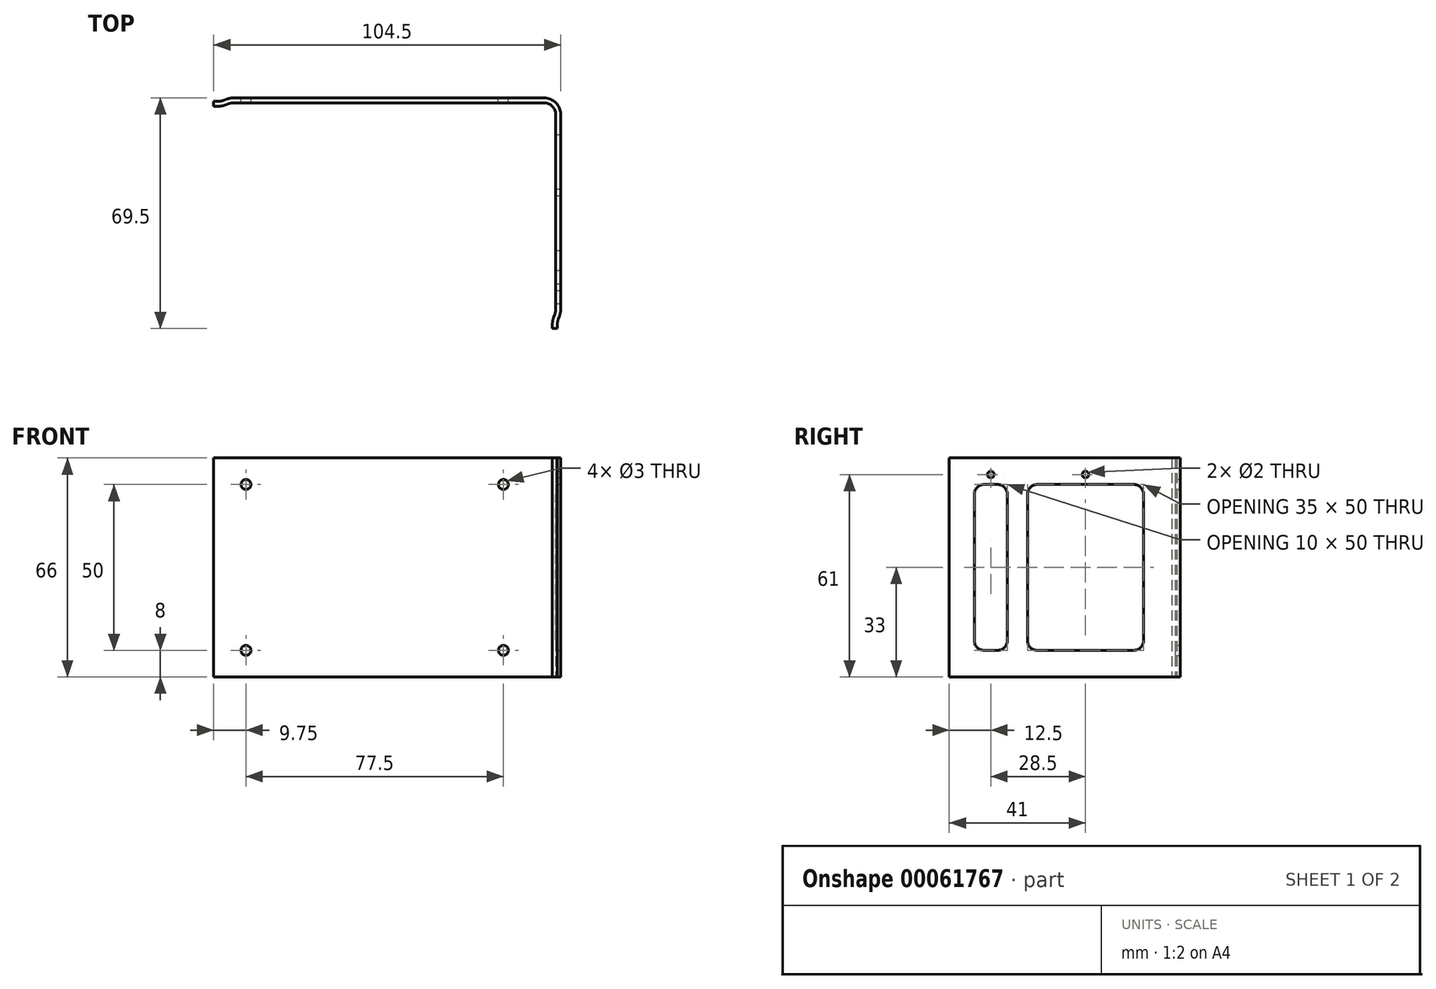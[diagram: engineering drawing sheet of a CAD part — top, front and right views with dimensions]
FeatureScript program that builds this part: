
annotation { "Feature Type Name" : "Feature", "Feature Type Description" : "" }
export const myFeature = defineFeature(function(context is Context, id is Id, definition is map)
    precondition{}
    {
        {
            var Q0;
            Q0=qCreatedBy(makeId("Top.planeOp"),FACE);
            var sketch = newSketch(context, id + "F0", { "sketchPlane" : qUnion([Q0])});
            skLineSegment(sketch, "E0", {"start": v(54.5, -26.49) * mm, "end": v(54.5, 33) * mm});
            skLineSegment(sketch, "E1", {"start": v(-46, 33) * mm, "end": v(-46, 0) * mm});
            skLineSegment(sketch, "E2.0", {"start": v(-47.5, 33) * mm, "end": v(-47.5, 0) * mm});
            skLineSegment(sketch, "E2.3", {"start": v(56, -26.75) * mm, "end": v(56, 33) * mm});
            skLineSegment(sketch, "E2.4", {"start": v(51, 38) * mm, "end": v(-42.5, 38) * mm});
            skLineSegment(sketch, "E3", {"start": v(-46, 0) * mm, "end": v(-47.5, 0) * mm});
            skPoint(sketch, "E4.visualSharp", {"position": v(54.5, 36.5) * mm});
            skArc(sketch, "E4.filletArc", {"start": v(54.5, 33) * mm, "mid": v(53.47, 35.47) * mm, "end": v(51, 36.5) * mm});
            skPoint(sketch, "E5.visualSharp", {"position": v(-46, 36.5) * mm});
            skArc(sketch, "E5.filletArc", {"start": v(-42.5, 36.5) * mm, "mid": v(-44.97, 35.47) * mm, "end": v(-46, 33) * mm});
            skPoint(sketch, "E6.visualSharp", {"position": v(56, 38) * mm});
            skArc(sketch, "E6.filletArc", {"start": v(56, 33) * mm, "mid": v(54.54, 36.54) * mm, "end": v(51, 38) * mm});
            skPoint(sketch, "E7.visualSharp", {"position": v(-47.5, 38) * mm});
            skArc(sketch, "E7.filletArc", {"start": v(-42.5, 38) * mm, "mid": v(-46.04, 36.54) * mm, "end": v(-47.5, 33) * mm});
            skLineSegment(sketch, "E8", {"start": v(54.5, 0) * mm, "end": v(-12.48, 0) * mm, "construction": true});
            skLineSegment(sketch, "E9", {"start": v(0, 36.5) * mm, "end": v(0, -15.2) * mm, "construction": true});
            skLineSegment(sketch, "E10", {"start": v(-42.5, 36.5) * mm, "end": v(51, 36.5) * mm});
            skLineSegment(sketch, "E11", {"start": v(55, -31.5) * mm, "end": v(55, -29.5) * mm});
            skLineSegment(sketch, "E12", {"start": v(55, -29.5) * mm, "end": v(56, -26.75) * mm});
            skLineSegment(sketch, "E13", {"start": v(55, -31.5) * mm, "end": v(53.5, -31.5) * mm});
            skLineSegment(sketch, "E14", {"start": v(53.5, -31.5) * mm, "end": v(53.5, -29.24) * mm});
            skLineSegment(sketch, "E15", {"start": v(53.5, -29.24) * mm, "end": v(54.5, -26.49) * mm});
            skSolve(sketch);
        }
        {
            var Q0;
            Q0=qSketchRegion(id+"F0",true);
            extrude(context, id + "F1", {"entities" : qUnion([Q0]), "depth" : 66 * mm});
        }
        {
            var Q0;
            Q0=makeQuery(id+"F1.opExtrude","SWEPT_FACE",FACE,{"disambiguationData":[OSD([sQuery(id+"F0.wireOp",EDGE,"E2.4")])]});
            var sketch = newSketch(context, id + "F2", { "sketchPlane" : qUnion([Q0])});
            skCircle(sketch, "E16", {"center": v(-38.75, 58) * mm, "radius": 1.5 * mm});
            skLineSegment(sketch, "E17", {"start": v(-38.75, 58) * mm, "end": v(-38.75, 8) * mm, "construction": true});
            skLineSegment(sketch, "E18", {"start": v(-38.75, 8) * mm, "end": v(38.75, 8) * mm, "construction": true});
            skLineSegment(sketch, "E19", {"start": v(38.75, 8) * mm, "end": v(38.75, 58) * mm, "construction": true});
            skLineSegment(sketch, "E20", {"start": v(38.75, 58) * mm, "end": v(-38.75, 58) * mm, "construction": true});
            skCircle(sketch, "E21", {"center": v(-38.75, 8) * mm, "radius": 1.5 * mm});
            skCircle(sketch, "E22", {"center": v(38.75, 8) * mm, "radius": 1.5 * mm});
            skCircle(sketch, "E23", {"center": v(38.75, 58) * mm, "radius": 1.5 * mm});
            skLineSegment(sketch, "E24", {"start": v(0, 0) * mm, "end": v(0, 116) * mm, "construction": true});
            skPoint(sketch, "E24.endSnap0", {"position": v(0, 0) * mm});
            skPoint(sketch, "E25", {"position": v(0, 58) * mm});
            skCircle(sketch, "E26", {"center": v(38.75, 49.63) * mm, "radius": 1.5 * mm});
            skCircle(sketch, "E27", {"center": v(38.75, 16.38) * mm, "radius": 1.5 * mm});
            skLineSegment(sketch, "E28", {"start": v(36, 33) * mm, "end": v(27.19, 33) * mm, "construction": true});
            skSolve(sketch);
        }
        {
            var Q0;
            Q0=makeQuery(id+"F2.imprint","IMPRINT",FACE,{"disambiguationData":[TD([[makeQuery(id+"F2.imprint","IMPRINT",EDGE,{"derivedFrom":sQuery(id+"F2.wireOp",EDGE,"E16")}),1.0]])]});
            var Q1;
            Q1=makeQuery(id+"F2.imprint","IMPRINT",FACE,{"disambiguationData":[TD([[makeQuery(id+"F2.imprint","IMPRINT",EDGE,{"derivedFrom":sQuery(id+"F2.wireOp",EDGE,"E21")}),1.0]])]});
            var Q2;
            Q2=makeQuery(id+"F2.imprint","IMPRINT",FACE,{"disambiguationData":[TD([[makeQuery(id+"F2.imprint","IMPRINT",EDGE,{"derivedFrom":sQuery(id+"F2.wireOp",EDGE,"E22")}),1.0]])]});
            var Q3;
            Q3=makeQuery(id+"F2.imprint","IMPRINT",FACE,{"disambiguationData":[TD([[makeQuery(id+"F2.imprint","IMPRINT",EDGE,{"derivedFrom":sQuery(id+"F2.wireOp",EDGE,"E23")}),1.0]])]});
            extrude(context, id + "F3", {"entities" : qUnion([Q0, Q1, Q2, Q3]), "operationType" : NewBodyOperationType.REMOVE, "oppositeDirection" : true, "depth" : 25 * mm});
        }
        {
            var Q0;
            Q0=makeQuery(id+"F1.opExtrude","SWEPT_FACE",FACE,{"disambiguationData":[OSD([sQuery(id+"F0.wireOp",EDGE,"E2.3")])]});
            var sketch = newSketch(context, id + "F4", { "sketchPlane" : qUnion([Q0])});
            skLineSegment(sketch, "E29.bottom", {"start": v(-21, 58) * mm, "end": v(-17, 58) * mm});
            skLineSegment(sketch, "E29.top", {"start": v(-21, 8) * mm, "end": v(-17, 8) * mm});
            skLineSegment(sketch, "E29.left", {"start": v(-24, 55) * mm, "end": v(-24, 11) * mm});
            skLineSegment(sketch, "E29.right", {"start": v(-14, 55) * mm, "end": v(-14, 11) * mm});
            skLineSegment(sketch, "E30.bottom", {"start": v(-5, 58) * mm, "end": v(24, 58) * mm});
            skLineSegment(sketch, "E30.top", {"start": v(-5, 8) * mm, "end": v(24, 8) * mm});
            skLineSegment(sketch, "E30.left", {"start": v(-8, 55) * mm, "end": v(-8, 11) * mm});
            skLineSegment(sketch, "E30.right", {"start": v(27, 55) * mm, "end": v(27, 11) * mm});
            skLineSegment(sketch, "E31", {"start": v(-14, 58) * mm, "end": v(-8, 58) * mm, "construction": true});
            skLineSegment(sketch, "E32", {"start": v(-14, 8) * mm, "end": v(-8, 8) * mm, "construction": true});
            skPoint(sketch, "E33.visualSharp", {"position": v(-24, 58) * mm});
            skArc(sketch, "E33.filletArc", {"start": v(-21, 58) * mm, "mid": v(-23.12, 57.12) * mm, "end": v(-24, 55) * mm});
            skPoint(sketch, "E34.visualSharp", {"position": v(-14, 58) * mm});
            skArc(sketch, "E34.filletArc", {"start": v(-14, 55) * mm, "mid": v(-14.88, 57.12) * mm, "end": v(-17, 58) * mm});
            skPoint(sketch, "E35.visualSharp", {"position": v(-24, 8) * mm});
            skArc(sketch, "E35.filletArc", {"start": v(-24, 11) * mm, "mid": v(-23.12, 8.88) * mm, "end": v(-21, 8) * mm});
            skPoint(sketch, "E36.visualSharp", {"position": v(-14, 8) * mm});
            skArc(sketch, "E36.filletArc", {"start": v(-17, 8) * mm, "mid": v(-14.88, 8.88) * mm, "end": v(-14, 11) * mm});
            skPoint(sketch, "E37.visualSharp", {"position": v(-8, 8) * mm});
            skArc(sketch, "E37.filletArc", {"start": v(-8, 11) * mm, "mid": v(-7.12, 8.88) * mm, "end": v(-5, 8) * mm});
            skPoint(sketch, "E38.visualSharp", {"position": v(27, 8) * mm});
            skArc(sketch, "E38.filletArc", {"start": v(24, 8) * mm, "mid": v(26.12, 8.88) * mm, "end": v(27, 11) * mm});
            skPoint(sketch, "E39.visualSharp", {"position": v(27, 58) * mm});
            skArc(sketch, "E39.filletArc", {"start": v(27, 55) * mm, "mid": v(26.12, 57.12) * mm, "end": v(24, 58) * mm});
            skPoint(sketch, "E40.visualSharp", {"position": v(-8, 58) * mm});
            skArc(sketch, "E40.filletArc", {"start": v(-5, 58) * mm, "mid": v(-7.12, 57.12) * mm, "end": v(-8, 55) * mm});
            skCircle(sketch, "E41", {"center": v(-19, 61) * mm, "radius": 1 * mm});
            skLineSegment(sketch, "E42", {"start": v(-24, 33) * mm, "end": v(27, 33) * mm, "construction": true});
            skLineSegment(sketch, "E43", {"start": v(-19, 58) * mm, "end": v(-19, 8) * mm, "construction": true});
            skPoint(sketch, "E43.endSnap0", {"position": v(-19, 8) * mm});
            skLineSegment(sketch, "E44", {"start": v(9.5, 8) * mm, "end": v(9.5, 58) * mm, "construction": true});
            skCircle(sketch, "E45", {"center": v(9.5, 61) * mm, "radius": 1 * mm});
            skCircle(sketch, "E46.MirrorC", {"center": v(-19, 5) * mm, "radius": 1 * mm});
            skCircle(sketch, "E47.MirrorC", {"center": v(9.5, 5) * mm, "radius": 1 * mm});
            skSolve(sketch);
        }
        {
            var Q0;
            Q0=makeQuery(id+"F4.imprint","IMPRINT",FACE,{"disambiguationData":[TD([[makeQuery(id+"F4.imprint","IMPRINT",EDGE,{"derivedFrom":sQuery(id+"F4.wireOp",EDGE,"E29.bottom")}),-1.0]])]});
            var Q1;
            Q1=makeQuery(id+"F4.imprint","IMPRINT",FACE,{"disambiguationData":[TD([[makeQuery(id+"F4.imprint","IMPRINT",EDGE,{"derivedFrom":sQuery(id+"F4.wireOp",EDGE,"E30.bottom")}),-1.0]])]});
            var Q2;
            Q2=makeQuery(id+"F4.imprint","IMPRINT",FACE,{"disambiguationData":[TD([[makeQuery(id+"F4.imprint","IMPRINT",EDGE,{"derivedFrom":sQuery(id+"F4.wireOp",EDGE,"E29.bottom")}),-1.0]])]});
            var Q3;
            Q3=makeQuery(id+"F4.imprint","IMPRINT",FACE,{"disambiguationData":[TD([[makeQuery(id+"F4.imprint","IMPRINT",EDGE,{"derivedFrom":sQuery(id+"F4.wireOp",EDGE,"E30.bottom")}),-1.0]])]});
            var Q4;
            Q4=makeQuery(id+"F4.imprint","IMPRINT",FACE,{"disambiguationData":[TD([[makeQuery(id+"F4.imprint","IMPRINT",EDGE,{"derivedFrom":sQuery(id+"F4.wireOp",EDGE,"E41")}),1.0]])]});
            var Q5;
            Q5=makeQuery(id+"F4.imprint","IMPRINT",FACE,{"disambiguationData":[TD([[makeQuery(id+"F4.imprint","IMPRINT",EDGE,{"derivedFrom":sQuery(id+"F4.wireOp",EDGE,"E45")}),1.0]])]});
            var Q6;
            Q6=makeQuery(id+"F4.imprint","IMPRINT",FACE,{"disambiguationData":[TD([[makeQuery(id+"F4.imprint","IMPRINT",EDGE,{"derivedFrom":sQuery(id+"F4.wireOp",EDGE,"E47.MirrorC")}),-1.0]])]});
            var Q7;
            Q7=makeQuery(id+"F4.imprint","IMPRINT",FACE,{"disambiguationData":[TD([[makeQuery(id+"F4.imprint","IMPRINT",EDGE,{"derivedFrom":sQuery(id+"F4.wireOp",EDGE,"E46.MirrorC")}),-1.0]])]});
            extrude(context, id + "F5", {"entities" : qUnion([Q0, Q1, Q2, Q3, Q4, Q5, Q6, Q7]), "operationType" : NewBodyOperationType.REMOVE, "oppositeDirection" : true, "depth" : 25 * mm});
        }
        {
            var Q0;
            Q0=makeQuery(id+"F1.opExtrude","SWEPT_EDGE",EDGE,{"disambiguationData":[OSD([sQuery(id+"F0.wireOp",EDGE,"E11"),sQuery(id+"F0.wireOp",EDGE,"E12")])]});
            var Q1;
            Q1=makeQuery(id+"F1.opExtrude","SWEPT_EDGE",EDGE,{"disambiguationData":[OSD([sQuery(id+"F0.wireOp",EDGE,"E0"),sQuery(id+"F0.wireOp",EDGE,"E15")])]});
            fillet(context, id + "F6", {"entities" : qUnion([Q0, Q1]), "radius" : 5 * mm, "tangentPropagation" : true, "allowEdgeOverflow" : false});
        }
        {
            var Q0;
            Q0=makeQuery(id+"F1.opExtrude","SWEPT_EDGE",EDGE,{"disambiguationData":[OSD([sQuery(id+"F0.wireOp",EDGE,"E2.3"),sQuery(id+"F0.wireOp",EDGE,"E12")])]});
            var Q1;
            Q1=makeQuery(id+"F1.opExtrude","SWEPT_EDGE",EDGE,{"disambiguationData":[OSD([sQuery(id+"F0.wireOp",EDGE,"E14"),sQuery(id+"F0.wireOp",EDGE,"E15")])]});
            fillet(context, id + "F7", {"entities" : qUnion([Q0, Q1]), "radius" : 6.5 * mm, "tangentPropagation" : true, "allowEdgeOverflow" : false});
        }
        {
            var Q0;
            Q0=qCreatedBy(makeId("Top.planeOp"),FACE);
            var sketch = newSketch(context, id + "F8", { "sketchPlane" : qUnion([Q0])});
            skLineSegment(sketch, "E48.bottom", {"start": v(-49.5, 43) * mm, "end": v(-42.5, 43) * mm});
            skLineSegment(sketch, "E48.top", {"start": v(-49.5, -5) * mm, "end": v(-42.5, -5) * mm});
            skLineSegment(sketch, "E48.left", {"start": v(-49.5, 43) * mm, "end": v(-49.5, -5) * mm});
            skLineSegment(sketch, "E48.right", {"start": v(-42.5, 43) * mm, "end": v(-42.5, -5) * mm});
            skSolve(sketch);
        }
        {
            var Q0;
            Q0=makeQuery(id+"F8.imprint","IMPRINT",FACE,{"disambiguationData":[TD([[makeQuery(id+"F8.imprint","IMPRINT",EDGE,{"derivedFrom":sQuery(id+"F8.wireOp",EDGE,"E48.bottom")}),-1.0]])]});
            extrude(context, id + "F9", {"entities" : qUnion([Q0]), "operationType" : NewBodyOperationType.REMOVE, "depth" : 100 * mm});
        }
        {
            var Q0;
            Q0=qCreatedBy(makeId("Top.planeOp"),FACE);
            var sketch = newSketch(context, id + "F10", { "sketchPlane" : qUnion([Q0])});
            skLineSegment(sketch, "E49", {"start": v(-48.5, 35.5) * mm, "end": v(-46.75, 35.5) * mm});
            skLineSegment(sketch, "E50", {"start": v(-45.04, 35.8) * mm, "end": v(-43.7, 36.29) * mm});
            skLineSegment(sketch, "E51", {"start": v(-44.21, 37.7) * mm, "end": v(-45.55, 37.21) * mm});
            skLineSegment(sketch, "E52", {"start": v(-46.75, 37) * mm, "end": v(-48.5, 37) * mm});
            skLineSegment(sketch, "E53", {"start": v(-48.5, 37) * mm, "end": v(-48.5, 35.5) * mm});
            skPoint(sketch, "E54.visualSharp", {"position": v(-46.13, 37) * mm});
            skArc(sketch, "E54.filletArc", {"start": v(-46.75, 37) * mm, "mid": v(-46.14, 37.05) * mm, "end": v(-45.55, 37.21) * mm});
            skPoint(sketch, "E55.visualSharp", {"position": v(-45.86, 35.5) * mm});
            skArc(sketch, "E55.filletArc", {"start": v(-46.75, 35.5) * mm, "mid": v(-45.88, 35.58) * mm, "end": v(-45.04, 35.8) * mm});
            skLineSegment(sketch, "E56", {"start": v(-42.5, 36.5) * mm, "end": v(-42.5, 36.5) * mm});
            skLineSegment(sketch, "E57", {"start": v(-42.5, 36.5) * mm, "end": v(-42.5, 38) * mm});
            skLineSegment(sketch, "E58", {"start": v(-42.5, 38) * mm, "end": v(-42.5, 38) * mm});
            skPoint(sketch, "E59.visualSharp", {"position": v(-43.38, 38) * mm});
            skArc(sketch, "E59.filletArc", {"start": v(-42.5, 38) * mm, "mid": v(-43.37, 37.92) * mm, "end": v(-44.21, 37.7) * mm});
            skPoint(sketch, "E60.visualSharp", {"position": v(-43.12, 36.5) * mm});
            skArc(sketch, "E60.filletArc", {"start": v(-42.5, 36.5) * mm, "mid": v(-43.1, 36.45) * mm, "end": v(-43.7, 36.29) * mm});
            skSolve(sketch);
        }
        {
            var Q0;
            Q0=makeQuery(id+"F10.imprint","IMPRINT",FACE,{"disambiguationData":[TD([[makeQuery(id+"F10.imprint","IMPRINT",EDGE,{"derivedFrom":sQuery(id+"F10.wireOp",EDGE,"E49")}),1.0]])]});
            extrude(context, id + "F11", {"entities" : qUnion([Q0]), "operationType" : NewBodyOperationType.ADD, "depth" : 66 * mm});
        }
    });
